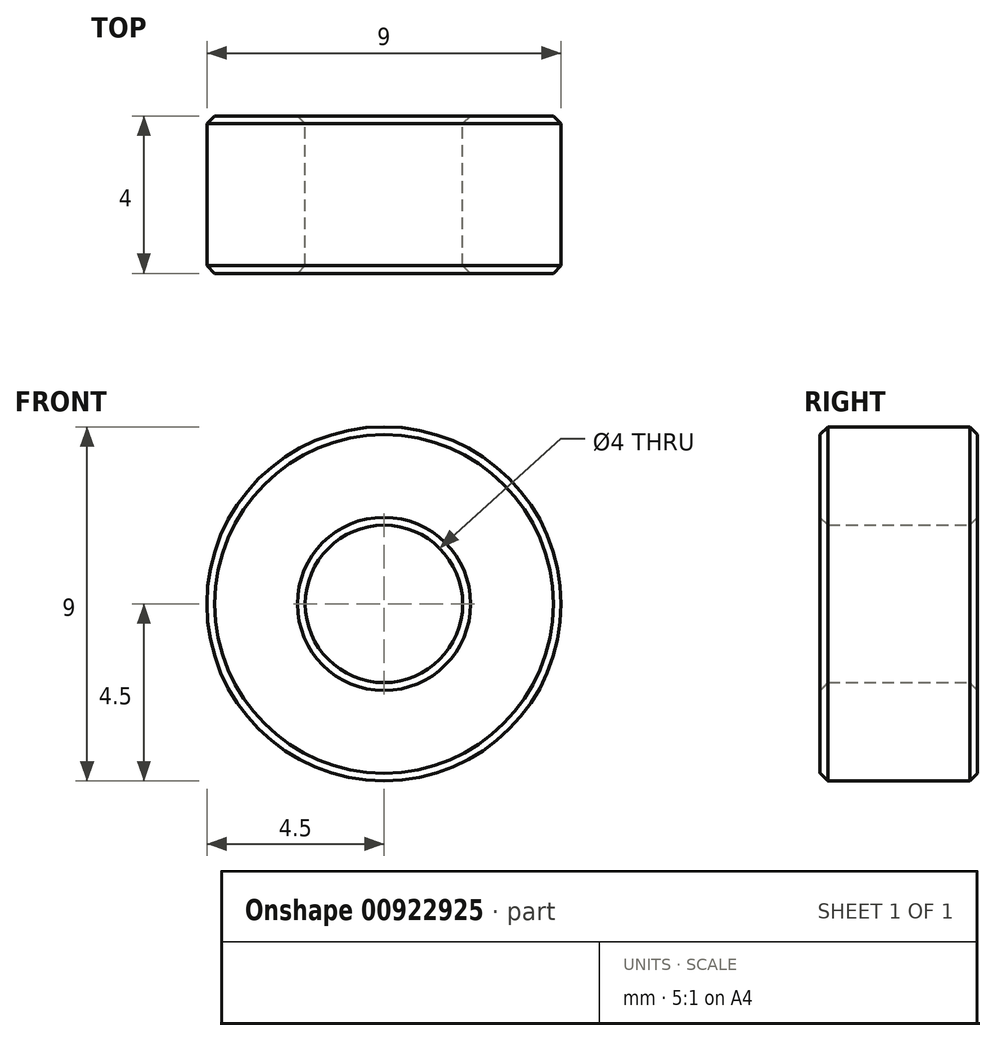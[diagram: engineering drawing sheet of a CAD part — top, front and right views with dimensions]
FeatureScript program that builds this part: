
annotation { "Feature Type Name" : "Feature", "Feature Type Description" : "" }
export const myFeature = defineFeature(function(context is Context, id is Id, definition is map)
    precondition{}
    {
        {
            var Q0;
            Q0=qCreatedBy(makeId("Front.planeOp"),FACE);
            var sketch = newSketch(context, id + "F0", { "sketchPlane" : qUnion([Q0])});
            skCircle(sketch, "E0", {"center": v(0, 0) * mm, "radius": 4.5 * mm});
            skCircle(sketch, "E1", {"center": v(0, 0) * mm, "radius": 2 * mm});
            skSolve(sketch);
        }
        {
            var Q0;
            Q0=makeQuery(id+"F0.imprint","IMPRINT",FACE,{"disambiguationData":[TD([[makeQuery(id+"F0.imprint","IMPRINT",EDGE,{"derivedFrom":sQuery(id+"F0.wireOp",EDGE,"E0")}),1.0]])]});
            extrude(context, id + "F1", {"entities" : qUnion([Q0]), "depth" : 4 * mm, "offsetDistance" : 25 * mm});
        }
        {
            var Q0;
            Q0=makeQuery(id+"F1.opExtrude","CAP_EDGE",EDGE,{"disambiguationData":[OSD([sQuery(id+"F0.wireOp",EDGE,"E0")])],"isStart":false});
            var Q1;
            Q1=makeQuery(id+"F1.opExtrude","CAP_EDGE",EDGE,{"disambiguationData":[OSD([sQuery(id+"F0.wireOp",EDGE,"E0")])],"isStart":true});
            var Q2;
            Q2=makeQuery(id+"F1.opExtrude","CAP_EDGE",EDGE,{"disambiguationData":[OSD([sQuery(id+"F0.wireOp",EDGE,"E1")])],"isStart":false});
            var Q3;
            Q3=makeQuery(id+"F1.opExtrude","CAP_EDGE",EDGE,{"disambiguationData":[OSD([sQuery(id+"F0.wireOp",EDGE,"E1")])],"isStart":true});
            chamfer(context, id + "F2", {"entities" : qUnion([Q0, Q1, Q2, Q3]), "width" : 0.2 * mm, "tangentPropagation" : true});
        }
    });
